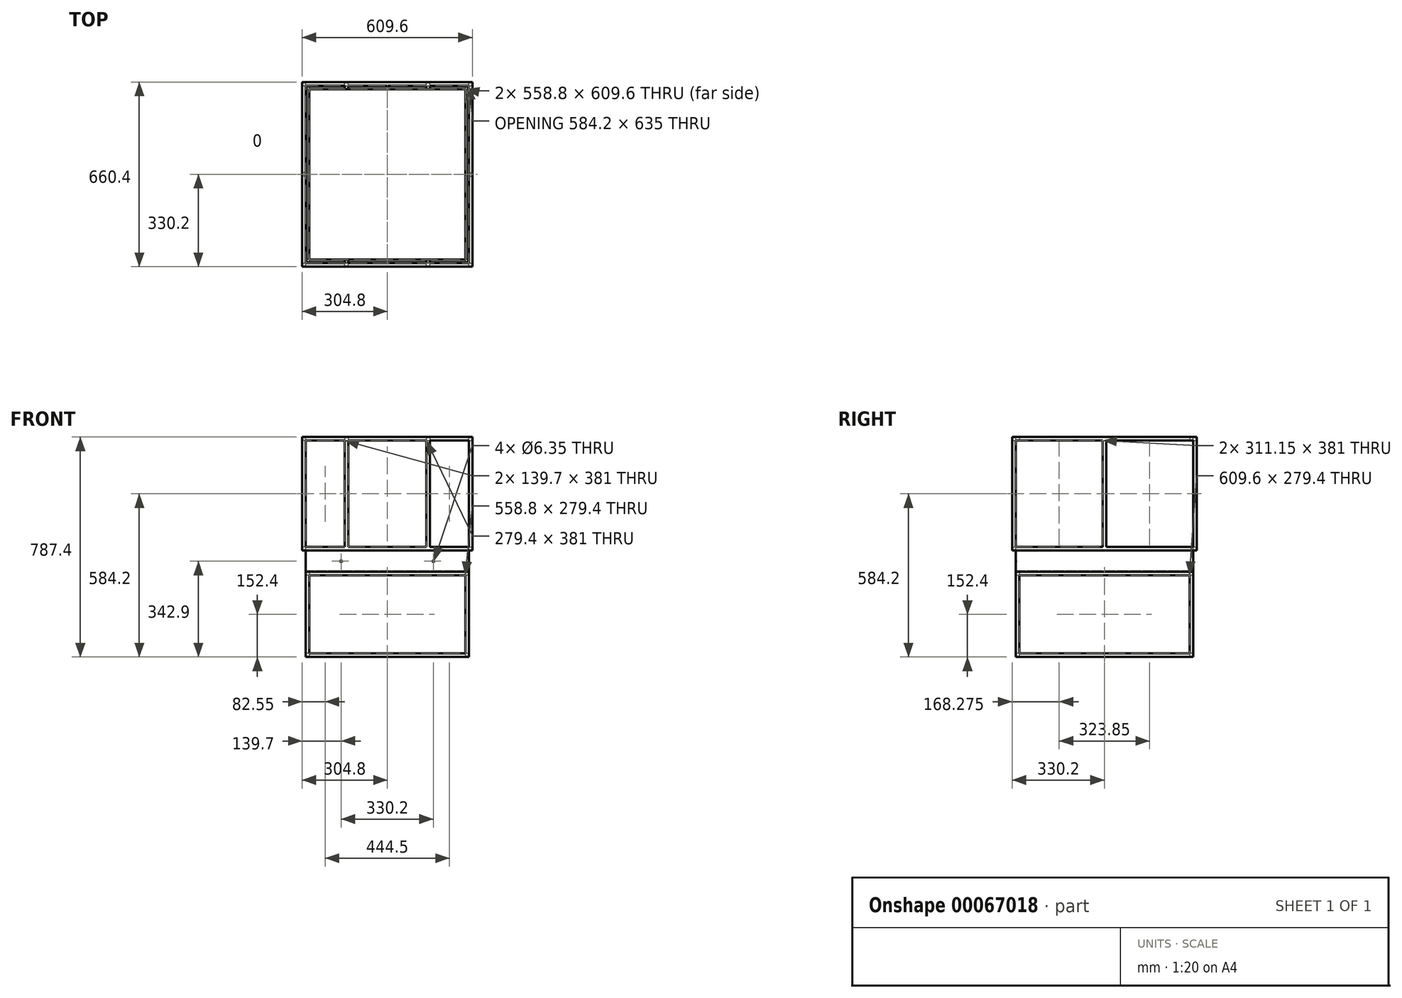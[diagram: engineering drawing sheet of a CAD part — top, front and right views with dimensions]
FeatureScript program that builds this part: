
annotation { "Feature Type Name" : "Feature", "Feature Type Description" : "" }
export const myFeature = defineFeature(function(context is Context, id is Id, definition is map)
    precondition{}
    {
        {
            var Q0;
            Q0=qCreatedBy(makeId("Front.planeOp"),FACE);
            var sketch = newSketch(context, id + "F0", { "sketchPlane" : qUnion([Q0])});
            skLineSegment(sketch, "E0.bottom", {"start": v(0, 0) * mm, "end": v(-609.6, 0) * mm});
            skLineSegment(sketch, "E0.top", {"start": v(0, 406.4) * mm, "end": v(-609.6, 406.4) * mm});
            skLineSegment(sketch, "E0.left", {"start": v(0, 0) * mm, "end": v(0, 406.4) * mm});
            skLineSegment(sketch, "E0.right", {"start": v(-609.6, 0) * mm, "end": v(-609.6, 406.4) * mm});
            skLineSegment(sketch, "E1.bottom", {"start": v(-596.9, 393.7) * mm, "end": v(-457.2, 393.7) * mm});
            skLineSegment(sketch, "E1.top", {"start": v(-596.9, 12.7) * mm, "end": v(-457.2, 12.7) * mm});
            skLineSegment(sketch, "E1.left", {"start": v(-596.9, 393.7) * mm, "end": v(-596.9, 12.7) * mm});
            skLineSegment(sketch, "E1.right", {"start": v(-457.2, 393.7) * mm, "end": v(-457.2, 12.7) * mm});
            skLineSegment(sketch, "E2.bottom", {"start": v(-444.5, 393.7) * mm, "end": v(-165.1, 393.7) * mm});
            skLineSegment(sketch, "E2.top", {"start": v(-444.5, 12.7) * mm, "end": v(-165.1, 12.7) * mm});
            skLineSegment(sketch, "E2.left", {"start": v(-444.5, 393.7) * mm, "end": v(-444.5, 12.7) * mm});
            skLineSegment(sketch, "E2.right", {"start": v(-165.1, 393.7) * mm, "end": v(-165.1, 12.7) * mm});
            skLineSegment(sketch, "E3.bottom", {"start": v(-152.4, 393.7) * mm, "end": v(-12.7, 393.7) * mm});
            skLineSegment(sketch, "E3.top", {"start": v(-152.4, 12.7) * mm, "end": v(-12.7, 12.7) * mm});
            skLineSegment(sketch, "E3.left", {"start": v(-152.4, 393.7) * mm, "end": v(-152.4, 12.7) * mm});
            skLineSegment(sketch, "E3.right", {"start": v(-12.7, 393.7) * mm, "end": v(-12.7, 12.7) * mm});
            skSolve(sketch);
        }
        {
            var Q0;
            Q0=makeQuery(id+"F0.imprint","IMPRINT",FACE,{"disambiguationData":[TD([[makeQuery(id+"F0.imprint","IMPRINT",EDGE,{"derivedFrom":sQuery(id+"F0.wireOp",EDGE,"E0.bottom")}),-1.0]])]});
            extrude(context, id + "F1", {"entities" : qUnion([Q0]), "depth" : 660.4 * mm});
        }
        {
            var Q0;
            Q0=makeQuery(id+"F1.opExtrude","SWEPT_FACE",FACE,{"disambiguationData":[OSD([sQuery(id+"F0.wireOp",EDGE,"E0.top")])]});
            var sketch = newSketch(context, id + "F2", { "sketchPlane" : qUnion([Q0])});
            skLineSegment(sketch, "E4.0", {"start": v(-596.9, -660.4) * mm, "end": v(-596.9, 0) * mm});
            skLineSegment(sketch, "E4.1", {"start": v(-444.5, -660.4) * mm, "end": v(-444.5, 0) * mm});
            skLineSegment(sketch, "E4.2", {"start": v(-152.4, -660.4) * mm, "end": v(-152.4, 0) * mm});
            skLineSegment(sketch, "E4.3", {"start": v(-457.2, -660.4) * mm, "end": v(-457.2, 0) * mm});
            skLineSegment(sketch, "E4.4", {"start": v(-165.1, -660.4) * mm, "end": v(-165.1, 0) * mm});
            skLineSegment(sketch, "E4.5", {"start": v(-12.7, -660.4) * mm, "end": v(-12.7, 0) * mm});
            skLineSegment(sketch, "E4.6", {"start": v(-609.6, -660.4) * mm, "end": v(-609.6, 0) * mm});
            skLineSegment(sketch, "E4.7", {"start": v(0, -660.4) * mm, "end": v(-609.6, -660.4) * mm});
            skLineSegment(sketch, "E4.8", {"start": v(0, -660.4) * mm, "end": v(0, 0) * mm});
            skLineSegment(sketch, "E4.9", {"start": v(0, 0) * mm, "end": v(-609.6, 0) * mm});
            skLineSegment(sketch, "E5", {"start": v(-609.6, -12.7) * mm, "end": v(0, -12.7) * mm});
            skLineSegment(sketch, "E6", {"start": v(-609.6, -647.7) * mm, "end": v(0, -647.7) * mm});
            skLineSegment(sketch, "E7", {"start": v(-609.6, -165.1) * mm, "end": v(0, -165.1) * mm});
            skLineSegment(sketch, "E8", {"start": v(-609.6, -495.3) * mm, "end": v(0, -495.3) * mm});
            skLineSegment(sketch, "E9", {"start": v(-609.6, -177.8) * mm, "end": v(0, -177.8) * mm});
            skLineSegment(sketch, "E10", {"start": v(-609.6, -482.6) * mm, "end": v(0, -482.6) * mm});
            skSolve(sketch);
        }
        {
            var Q0;
            {var subQ0=sQuery(id+"F2.wireOp",EDGE,"E7");var subQ1=sQuery(id+"F2.wireOp",EDGE,"E4.0");var subQ2=makeQuery(id+"F2.imprint","INTERSECT",VERTEX,{"derivedFrom":[subQ1,subQ0]});Q0=makeQuery(id+"F2.imprint","IMPRINT",FACE,{"disambiguationData":[TD([[makeQuery(id+"F2.imprint","IMPRINT",EDGE,{"disambiguationData":[TD([[subQ2,-1.0]])],"derivedFrom":subQ1}),-1.0]])]});}
            var Q1;
            {var subQ0=sQuery(id+"F2.wireOp",EDGE,"E7");var subQ1=sQuery(id+"F2.wireOp",EDGE,"E4.1");var subQ2=makeQuery(id+"F2.imprint","INTERSECT",VERTEX,{"derivedFrom":[subQ1,subQ0]});Q1=makeQuery(id+"F2.imprint","IMPRINT",FACE,{"disambiguationData":[TD([[makeQuery(id+"F2.imprint","IMPRINT",EDGE,{"disambiguationData":[TD([[subQ2,-1.0]])],"derivedFrom":subQ1}),-1.0]])]});}
            var Q2;
            {var subQ0=sQuery(id+"F2.wireOp",EDGE,"E7");var subQ1=sQuery(id+"F2.wireOp",EDGE,"E4.2");var subQ2=makeQuery(id+"F2.imprint","INTERSECT",VERTEX,{"derivedFrom":[subQ1,subQ0]});Q2=makeQuery(id+"F2.imprint","IMPRINT",FACE,{"disambiguationData":[TD([[makeQuery(id+"F2.imprint","IMPRINT",EDGE,{"disambiguationData":[TD([[subQ2,-1.0]])],"derivedFrom":subQ1}),-1.0]])]});}
            var Q3;
            {var subQ0=sQuery(id+"F2.wireOp",EDGE,"E10");var subQ1=sQuery(id+"F2.wireOp",EDGE,"E4.2");var subQ2=makeQuery(id+"F2.imprint","INTERSECT",VERTEX,{"derivedFrom":[subQ1,subQ0]});Q3=makeQuery(id+"F2.imprint","IMPRINT",FACE,{"disambiguationData":[TD([[makeQuery(id+"F2.imprint","IMPRINT",EDGE,{"disambiguationData":[TD([[subQ2,-1.0]])],"derivedFrom":subQ1}),-1.0]])]});}
            var Q4;
            {var subQ0=sQuery(id+"F2.wireOp",EDGE,"E10");var subQ1=sQuery(id+"F2.wireOp",EDGE,"E4.1");var subQ2=makeQuery(id+"F2.imprint","INTERSECT",VERTEX,{"derivedFrom":[subQ1,subQ0]});Q4=makeQuery(id+"F2.imprint","IMPRINT",FACE,{"disambiguationData":[TD([[makeQuery(id+"F2.imprint","IMPRINT",EDGE,{"disambiguationData":[TD([[subQ2,-1.0]])],"derivedFrom":subQ1}),-1.0]])]});}
            var Q5;
            {var subQ0=sQuery(id+"F2.wireOp",EDGE,"E10");var subQ1=sQuery(id+"F2.wireOp",EDGE,"E4.0");var subQ2=makeQuery(id+"F2.imprint","INTERSECT",VERTEX,{"derivedFrom":[subQ1,subQ0]});Q5=makeQuery(id+"F2.imprint","IMPRINT",FACE,{"disambiguationData":[TD([[makeQuery(id+"F2.imprint","IMPRINT",EDGE,{"disambiguationData":[TD([[subQ2,-1.0]])],"derivedFrom":subQ1}),-1.0]])]});}
            var Q6;
            {var subQ0=sQuery(id+"F2.wireOp",EDGE,"E6");var subQ1=sQuery(id+"F2.wireOp",EDGE,"E4.0");var subQ2=makeQuery(id+"F2.imprint","INTERSECT",VERTEX,{"derivedFrom":[subQ1,subQ0]});Q6=makeQuery(id+"F2.imprint","IMPRINT",FACE,{"disambiguationData":[TD([[makeQuery(id+"F2.imprint","IMPRINT",EDGE,{"disambiguationData":[TD([[subQ2,-1.0]])],"derivedFrom":subQ1}),-1.0]])]});}
            var Q7;
            {var subQ0=sQuery(id+"F2.wireOp",EDGE,"E6");var subQ1=sQuery(id+"F2.wireOp",EDGE,"E4.1");var subQ2=makeQuery(id+"F2.imprint","INTERSECT",VERTEX,{"derivedFrom":[subQ1,subQ0]});Q7=makeQuery(id+"F2.imprint","IMPRINT",FACE,{"disambiguationData":[TD([[makeQuery(id+"F2.imprint","IMPRINT",EDGE,{"disambiguationData":[TD([[subQ2,-1.0]])],"derivedFrom":subQ1}),-1.0]])]});}
            var Q8;
            {var subQ0=sQuery(id+"F2.wireOp",EDGE,"E6");var subQ1=sQuery(id+"F2.wireOp",EDGE,"E4.2");var subQ2=makeQuery(id+"F2.imprint","INTERSECT",VERTEX,{"derivedFrom":[subQ1,subQ0]});Q8=makeQuery(id+"F2.imprint","IMPRINT",FACE,{"disambiguationData":[TD([[makeQuery(id+"F2.imprint","IMPRINT",EDGE,{"disambiguationData":[TD([[subQ2,-1.0]])],"derivedFrom":subQ1}),-1.0]])]});}
            extrude(context, id + "F3", {"entities" : qUnion([Q0, Q1, Q2, Q3, Q4, Q5, Q6, Q7, Q8]), "operationType" : NewBodyOperationType.REMOVE, "endBound" : BoundingType.THROUGH_ALL, "oppositeDirection" : true, "depth" : 25.4 * mm});
        }
        {
            var Q0;
            Q0=makeQuery(id+"F1.opExtrude","SWEPT_FACE",FACE,{"disambiguationData":[OSD([sQuery(id+"F0.wireOp",EDGE,"E0.left")])]});
            var sketch = newSketch(context, id + "F4", { "sketchPlane" : qUnion([Q0])});
            skLineSegment(sketch, "E11.0.0", {"start": v(0, 393.7) * mm, "end": v(-12.7, 393.7) * mm});
            skLineSegment(sketch, "E11.0.1", {"start": v(-12.7, 393.7) * mm, "end": v(-12.7, 406.4) * mm});
            skLineSegment(sketch, "E11.0.2", {"start": v(-12.7, 406.4) * mm, "end": v(-165.1, 406.4) * mm});
            skLineSegment(sketch, "E11.0.3", {"start": v(-165.1, 406.4) * mm, "end": v(-165.1, 393.7) * mm});
            skLineSegment(sketch, "E11.0.4", {"start": v(-165.1, 393.7) * mm, "end": v(-177.8, 393.7) * mm});
            skLineSegment(sketch, "E11.0.5", {"start": v(-177.8, 393.7) * mm, "end": v(-177.8, 406.4) * mm});
            skLineSegment(sketch, "E11.0.6", {"start": v(-177.8, 406.4) * mm, "end": v(-482.6, 406.4) * mm});
            skLineSegment(sketch, "E11.0.7", {"start": v(-482.6, 406.4) * mm, "end": v(-482.6, 393.7) * mm});
            skLineSegment(sketch, "E11.0.8", {"start": v(-482.6, 393.7) * mm, "end": v(-495.3, 393.7) * mm});
            skLineSegment(sketch, "E11.0.9", {"start": v(-495.3, 393.7) * mm, "end": v(-495.3, 406.4) * mm});
            skLineSegment(sketch, "E11.0.10", {"start": v(-495.3, 406.4) * mm, "end": v(-647.7, 406.4) * mm});
            skLineSegment(sketch, "E11.0.11", {"start": v(-647.7, 406.4) * mm, "end": v(-647.7, 393.7) * mm});
            skLineSegment(sketch, "E11.0.12", {"start": v(-647.7, 393.7) * mm, "end": v(-660.4, 393.7) * mm});
            skLineSegment(sketch, "E11.0.13", {"start": v(-660.4, 393.7) * mm, "end": v(-660.4, 12.7) * mm});
            skLineSegment(sketch, "E11.0.14", {"start": v(-660.4, 12.7) * mm, "end": v(-647.7, 12.7) * mm});
            skLineSegment(sketch, "E11.0.15", {"start": v(-647.7, 12.7) * mm, "end": v(-647.7, 0) * mm});
            skLineSegment(sketch, "E11.0.16", {"start": v(-647.7, 0) * mm, "end": v(-495.3, 0) * mm});
            skLineSegment(sketch, "E11.0.17", {"start": v(-495.3, 0) * mm, "end": v(-495.3, 12.7) * mm});
            skLineSegment(sketch, "E11.0.18", {"start": v(-495.3, 12.7) * mm, "end": v(-482.6, 12.7) * mm});
            skLineSegment(sketch, "E11.0.19", {"start": v(-482.6, 12.7) * mm, "end": v(-482.6, 0) * mm});
            skLineSegment(sketch, "E11.0.20", {"start": v(-482.6, 0) * mm, "end": v(-177.8, 0) * mm});
            skLineSegment(sketch, "E11.0.21", {"start": v(-177.8, 0) * mm, "end": v(-177.8, 12.7) * mm});
            skLineSegment(sketch, "E11.0.22", {"start": v(-177.8, 12.7) * mm, "end": v(-165.1, 12.7) * mm});
            skLineSegment(sketch, "E11.0.23", {"start": v(-165.1, 12.7) * mm, "end": v(-165.1, 0) * mm});
            skLineSegment(sketch, "E11.0.24", {"start": v(-165.1, 0) * mm, "end": v(-12.7, 0) * mm});
            skLineSegment(sketch, "E11.0.25", {"start": v(-12.7, 0) * mm, "end": v(-12.7, 12.7) * mm});
            skLineSegment(sketch, "E11.0.26", {"start": v(-12.7, 12.7) * mm, "end": v(0, 12.7) * mm});
            skLineSegment(sketch, "E11.0.27", {"start": v(0, 12.7) * mm, "end": v(0, 393.7) * mm});
            skLineSegment(sketch, "E12", {"start": v(-647.7, 393.7) * mm, "end": v(-12.7, 393.7) * mm});
            skLineSegment(sketch, "E13", {"start": v(-12.7, 393.7) * mm, "end": v(-12.7, 12.7) * mm});
            skLineSegment(sketch, "E14", {"start": v(-12.7, 12.7) * mm, "end": v(-647.7, 12.7) * mm});
            skLineSegment(sketch, "E15", {"start": v(-647.7, 12.7) * mm, "end": v(-647.7, 393.7) * mm});
            skLineSegment(sketch, "E16", {"start": v(-495.3, 393.7) * mm, "end": v(-495.3, 12.7) * mm});
            skLineSegment(sketch, "E17", {"start": v(-482.6, 12.7) * mm, "end": v(-482.6, 393.7) * mm});
            skLineSegment(sketch, "E18", {"start": v(-177.8, 393.7) * mm, "end": v(-177.8, 12.7) * mm});
            skLineSegment(sketch, "E19", {"start": v(-165.1, 393.7) * mm, "end": v(-165.1, 12.7) * mm});
            skSolve(sketch);
        }
        {
            var Q0;
            {var subQ2=sQuery(id+"F4.wireOp",EDGE,"E15");Q0=makeQuery(id+"F4.imprint","IMPRINT",FACE,{"disambiguationData":[TD([[makeQuery(id+"F4.imprint","IMPRINT",EDGE,{"derivedFrom":subQ2}),-1.0]])]});}
            var Q1;
            {var subQ2=sQuery(id+"F4.wireOp",EDGE,"E17");Q1=makeQuery(id+"F4.imprint","IMPRINT",FACE,{"disambiguationData":[TD([[makeQuery(id+"F4.imprint","IMPRINT",EDGE,{"derivedFrom":subQ2}),-1.0]])]});}
            var Q2;
            {var subQ0=sQuery(id+"F4.wireOp",EDGE,"E13");Q2=makeQuery(id+"F4.imprint","IMPRINT",FACE,{"disambiguationData":[TD([[makeQuery(id+"F4.imprint","IMPRINT",EDGE,{"derivedFrom":subQ0}),-1.0]])]});}
            extrude(context, id + "F5", {"entities" : qUnion([Q0, Q1, Q2]), "operationType" : NewBodyOperationType.REMOVE, "endBound" : BoundingType.THROUGH_ALL, "oppositeDirection" : true, "depth" : 25.4 * mm});
        }
        {
            var Q0;
            {var subQ1=sQuery(id+"F2.wireOp",EDGE,"E6");var subQ3=sQuery(id+"F2.wireOp",EDGE,"E8");var subQ6=makeQuery(id+"F1.opExtrude","SWEPT_FACE",FACE,{"disambiguationData":[OSD([sQuery(id+"F0.wireOp",EDGE,"E3.left")])]});var subQ7=sQuery(id+"F2.wireOp",EDGE,"E10");var subQ8=sQuery(id+"F2.wireOp",EDGE,"E4.2");var subQ9=makeQuery(id+"F2.imprint","INTERSECT",VERTEX,{"derivedFrom":[subQ8,subQ7]});var subQ11=makeQuery(id+"F3.opExtrude","SWEPT_FACE",FACE,{"disambiguationData":[OSD([subQ8]),TDD([makeQuery(id+"F2.imprint","IMPRINT",EDGE,{"disambiguationData":[TD([[subQ9,-1.0]])],"derivedFrom":subQ8})])]});var subQ12=makeQuery(id+"F1.opExtrude","SWEPT_FACE",FACE,{"disambiguationData":[OSD([sQuery(id+"F0.wireOp",EDGE,"E3.top")])]});var subQ13=makeQuery(id+"F1.opExtrude","SWEPT_FACE",FACE,{"disambiguationData":[OSD([sQuery(id+"F0.wireOp",EDGE,"E0.bottom")])]});var subQ16=makeQuery(id+"F2.imprint","INTERSECT",VERTEX,{"derivedFrom":[subQ8,subQ3]});var subQ17=makeQuery(id+"F3.opExtrude","SWEPT_FACE",FACE,{"disambiguationData":[OSD([subQ8]),TDD([makeQuery(id+"F2.imprint","IMPRINT",EDGE,{"disambiguationData":[TD([[makeQuery(id+"F2.imprint","INTERSECT",VERTEX,{"derivedFrom":[subQ8,subQ1]}),-1.0]])],"derivedFrom":subQ8})])]});var subQ18=sQuery(id+"F2.wireOp",EDGE,"E7");var subQ21=makeQuery(id+"F3.opExtrude","SWEPT_FACE",FACE,{"disambiguationData":[OSD([subQ8]),TDD([makeQuery(id+"F2.imprint","IMPRINT",EDGE,{"disambiguationData":[TD([[makeQuery(id+"F2.imprint","INTERSECT",VERTEX,{"derivedFrom":[subQ8,subQ18]}),-1.0]])],"derivedFrom":subQ8})])]});var subQ22=makeQuery(id+"F3.opExtrude","SWEPT_FACE",FACE,{"disambiguationData":[OSD([subQ7]),TDD([makeQuery(id+"F2.imprint","IMPRINT",EDGE,{"disambiguationData":[TD([[subQ9,-1.0]])],"derivedFrom":subQ7})])]});var subQ23=makeQuery(id+"F1.opExtrude","SWEPT_FACE",FACE,{"disambiguationData":[OSD([sQuery(id+"F0.wireOp",EDGE,"E3.bottom")])]});var subQ24=makeQuery(id+"F1.opExtrude","SWEPT_FACE",FACE,{"disambiguationData":[OSD([sQuery(id+"F0.wireOp",EDGE,"E0.top")])]});var subQ25=makeQuery(id+"F3.opExtrude","SWEPT_FACE",FACE,{"disambiguationData":[OSD([subQ3]),TDD([makeQuery(id+"F2.imprint","IMPRINT",EDGE,{"disambiguationData":[TD([[subQ16,-1.0]])],"derivedFrom":subQ3})])]});var subQ26=sQuery(id+"F4.wireOp",EDGE,"E17");var subQ27=sQuery(id+"F4.wireOp",EDGE,"E18");var subQ28=sQuery(id+"F4.wireOp",EDGE,"E12");var subQ30=sQuery(id+"F4.wireOp",EDGE,"E14");var subQ31=sQuery(id+"F4.wireOp",EDGE,"E16");Q0=makeQuery(id+"F5.boolean.opBoolean","SPLIT",FACE,{"disambiguationData":[TD([subQ23,subQ12,subQ6,subQ17,subQ11,subQ21,makeQuery(id+"F3.boolean.opBoolean","COPY",FACE,{"disambiguationData":[TD([subQ24])],"derivedFrom":subQ25}),makeQuery(id+"F3.boolean.opBoolean","COPY",FACE,{"disambiguationData":[TD([subQ13])],"derivedFrom":subQ25}),makeQuery(id+"F3.boolean.opBoolean","COPY",FACE,{"disambiguationData":[TD([subQ24])],"derivedFrom":subQ22}),makeQuery(id+"F3.boolean.opBoolean","COPY",FACE,{"disambiguationData":[TD([subQ13])],"derivedFrom":subQ22}),makeQuery(id+"F5.opExtrude","SWEPT_FACE",FACE,{"disambiguationData":[OSD([subQ28]),TDD([makeQuery(id+"F4.imprint","IMPRINT",EDGE,{"disambiguationData":[TD([[makeQuery(id+"F4.imprint","INTERSECT",VERTEX,{"derivedFrom":[sQuery(id+"F4.wireOp",EDGE,"E11.0.9"),subQ28,subQ31]}),1.0]])],"derivedFrom":subQ28})])]}),makeQuery(id+"F5.opExtrude","SWEPT_FACE",FACE,{"disambiguationData":[OSD([subQ28]),TDD([makeQuery(id+"F4.imprint","IMPRINT",EDGE,{"disambiguationData":[TD([[makeQuery(id+"F4.imprint","INTERSECT",VERTEX,{"derivedFrom":[sQuery(id+"F4.wireOp",EDGE,"E11.0.5"),subQ28,subQ27]}),1.0]])],"derivedFrom":subQ28})])]}),makeQuery(id+"F5.opExtrude","SWEPT_FACE",FACE,{"disambiguationData":[OSD([subQ30]),TDD([makeQuery(id+"F4.imprint","IMPRINT",EDGE,{"disambiguationData":[TD([[makeQuery(id+"F4.imprint","INTERSECT",VERTEX,{"derivedFrom":[sQuery(id+"F4.wireOp",EDGE,"E11.0.19"),subQ30,subQ26]}),1.0]])],"derivedFrom":subQ30})])]}),makeQuery(id+"F5.opExtrude","SWEPT_FACE",FACE,{"disambiguationData":[OSD([subQ30]),TDD([makeQuery(id+"F4.imprint","IMPRINT",EDGE,{"disambiguationData":[TD([[makeQuery(id+"F4.imprint","INTERSECT",VERTEX,{"derivedFrom":[sQuery(id+"F4.wireOp",EDGE,"E11.0.17"),subQ30,subQ31]}),-1.0]])],"derivedFrom":subQ30})])]}),makeQuery(id+"F5.opExtrude","SWEPT_FACE",FACE,{"disambiguationData":[OSD([subQ31])]}),makeQuery(id+"F5.opExtrude","SWEPT_FACE",FACE,{"disambiguationData":[OSD([subQ26])]})])],"derivedFrom":makeQuery(id+"F3.boolean.opBoolean","MERGE",FACE,{"derivedFrom":[subQ6,subQ17,subQ11,subQ21]})});}
            var sketch = newSketch(context, id + "F6", { "sketchPlane" : qUnion([Q0])});
            skPoint(sketch, "E20.0", {"position": v(-495.3, 12.7) * mm});
            skPoint(sketch, "E20.1", {"position": v(-482.6, 12.7) * mm});
            skLineSegment(sketch, "E20.2", {"start": v(-495.3, 393.7) * mm, "end": v(-495.3, 12.7) * mm});
            skLineSegment(sketch, "E20.3", {"start": v(-482.6, 12.7) * mm, "end": v(-482.6, 393.7) * mm});
            skLineSegment(sketch, "E20.4", {"start": v(-495.3, 12.7) * mm, "end": v(-482.6, 12.7) * mm});
            skLineSegment(sketch, "E20.5", {"start": v(-495.3, 393.7) * mm, "end": v(-482.6, 393.7) * mm});
            skLineSegment(sketch, "E21.0", {"start": v(-177.8, 393.7) * mm, "end": v(-165.1, 393.7) * mm});
            skLineSegment(sketch, "E21.1", {"start": v(-177.8, 393.7) * mm, "end": v(-177.8, 12.7) * mm});
            skLineSegment(sketch, "E21.2", {"start": v(-165.1, 393.7) * mm, "end": v(-165.1, 12.7) * mm});
            skLineSegment(sketch, "E21.3", {"start": v(-177.8, 12.7) * mm, "end": v(-165.1, 12.7) * mm});
            skSolve(sketch);
        }
        {
            var Q0;
            Q0=makeQuery(id+"F6.imprint","IMPRINT",FACE,{"disambiguationData":[TD([[makeQuery(id+"F6.imprint","IMPRINT",EDGE,{"derivedFrom":sQuery(id+"F6.wireOp",EDGE,"E20.2")}),1.0]])]});
            var Q1;
            Q1=makeQuery(id+"F6.imprint","IMPRINT",FACE,{"disambiguationData":[TD([[makeQuery(id+"F6.imprint","IMPRINT",EDGE,{"derivedFrom":sQuery(id+"F6.wireOp",EDGE,"E21.0")}),-1.0]])]});
            extrude(context, id + "F7", {"entities" : qUnion([Q0, Q1]), "operationType" : NewBodyOperationType.REMOVE, "oppositeDirection" : true, "depth" : 304.8 * mm});
        }
        {
            var Q0;
            Q0=makeQuery(id+"F1.opExtrude","SWEPT_FACE",FACE,{"disambiguationData":[OSD([sQuery(id+"F0.wireOp",EDGE,"E0.top")])]});
            var sketch = newSketch(context, id + "F8", { "sketchPlane" : qUnion([Q0])});
            skLineSegment(sketch, "E22.0", {"start": v(-596.9, -165.1) * mm, "end": v(-457.2, -165.1) * mm});
            skLineSegment(sketch, "E22.1", {"start": v(-596.9, -177.8) * mm, "end": v(-457.2, -177.8) * mm});
            skLineSegment(sketch, "E22.2", {"start": v(-444.5, -165.1) * mm, "end": v(-165.1, -165.1) * mm});
            skLineSegment(sketch, "E22.3", {"start": v(-444.5, -177.8) * mm, "end": v(-165.1, -177.8) * mm});
            skLineSegment(sketch, "E22.4", {"start": v(-152.4, -165.1) * mm, "end": v(-12.7, -165.1) * mm});
            skLineSegment(sketch, "E22.5", {"start": v(-152.4, -177.8) * mm, "end": v(-12.7, -177.8) * mm});
            skLineSegment(sketch, "E22.6", {"start": v(-596.9, -482.6) * mm, "end": v(-457.2, -482.6) * mm});
            skLineSegment(sketch, "E22.7", {"start": v(-596.9, -495.3) * mm, "end": v(-457.2, -495.3) * mm});
            skLineSegment(sketch, "E22.8", {"start": v(-444.5, -482.6) * mm, "end": v(-165.1, -482.6) * mm});
            skLineSegment(sketch, "E22.9", {"start": v(-444.5, -495.3) * mm, "end": v(-165.1, -495.3) * mm});
            skLineSegment(sketch, "E22.10", {"start": v(-152.4, -482.6) * mm, "end": v(-12.7, -482.6) * mm});
            skLineSegment(sketch, "E22.11", {"start": v(-152.4, -495.3) * mm, "end": v(-12.7, -495.3) * mm});
            skLineSegment(sketch, "E23", {"start": v(-596.9, -482.6) * mm, "end": v(-596.9, -495.3) * mm});
            skLineSegment(sketch, "E24", {"start": v(-457.2, -482.6) * mm, "end": v(-457.2, -495.3) * mm});
            skLineSegment(sketch, "E25", {"start": v(-444.5, -495.3) * mm, "end": v(-444.5, -482.6) * mm});
            skLineSegment(sketch, "E26", {"start": v(-165.1, -482.6) * mm, "end": v(-165.1, -495.3) * mm});
            skLineSegment(sketch, "E27", {"start": v(-152.4, -495.3) * mm, "end": v(-152.4, -482.6) * mm});
            skLineSegment(sketch, "E28", {"start": v(-12.7, -482.6) * mm, "end": v(-12.7, -495.3) * mm});
            skLineSegment(sketch, "E29", {"start": v(-596.9, -165.1) * mm, "end": v(-596.9, -177.8) * mm});
            skLineSegment(sketch, "E30", {"start": v(-457.2, -165.1) * mm, "end": v(-457.2, -177.8) * mm});
            skLineSegment(sketch, "E31", {"start": v(-444.5, -165.1) * mm, "end": v(-444.5, -177.8) * mm});
            skLineSegment(sketch, "E32", {"start": v(-165.1, -165.1) * mm, "end": v(-165.1, -177.8) * mm});
            skLineSegment(sketch, "E33", {"start": v(-152.4, -165.1) * mm, "end": v(-152.4, -177.8) * mm});
            skLineSegment(sketch, "E34", {"start": v(-12.7, -177.8) * mm, "end": v(-12.7, -165.1) * mm});
            skSolve(sketch);
        }
        {
            var Q0;
            Q0=makeQuery(id+"F8.imprint","IMPRINT",FACE,{"disambiguationData":[TD([[makeQuery(id+"F8.imprint","IMPRINT",EDGE,{"derivedFrom":sQuery(id+"F8.wireOp",EDGE,"E22.0")}),-1.0]])]});
            var Q1;
            Q1=makeQuery(id+"F8.imprint","IMPRINT",FACE,{"disambiguationData":[TD([[makeQuery(id+"F8.imprint","IMPRINT",EDGE,{"derivedFrom":sQuery(id+"F8.wireOp",EDGE,"E22.2")}),-1.0]])]});
            var Q2;
            Q2=makeQuery(id+"F8.imprint","IMPRINT",FACE,{"disambiguationData":[TD([[makeQuery(id+"F8.imprint","IMPRINT",EDGE,{"derivedFrom":sQuery(id+"F8.wireOp",EDGE,"E22.4")}),-1.0]])]});
            var Q3;
            Q3=makeQuery(id+"F8.imprint","IMPRINT",FACE,{"disambiguationData":[TD([[makeQuery(id+"F8.imprint","IMPRINT",EDGE,{"derivedFrom":sQuery(id+"F8.wireOp",EDGE,"E22.10")}),-1.0]])]});
            var Q4;
            Q4=makeQuery(id+"F8.imprint","IMPRINT",FACE,{"disambiguationData":[TD([[makeQuery(id+"F8.imprint","IMPRINT",EDGE,{"derivedFrom":sQuery(id+"F8.wireOp",EDGE,"E22.8")}),-1.0]])]});
            var Q5;
            Q5=makeQuery(id+"F8.imprint","IMPRINT",FACE,{"disambiguationData":[TD([[makeQuery(id+"F8.imprint","IMPRINT",EDGE,{"derivedFrom":sQuery(id+"F8.wireOp",EDGE,"E22.6")}),-1.0]])]});
            extrude(context, id + "F9", {"entities" : qUnion([Q0, Q1, Q2, Q3, Q4, Q5]), "operationType" : NewBodyOperationType.REMOVE, "endBound" : BoundingType.THROUGH_ALL, "oppositeDirection" : true, "depth" : 25.4 * mm});
        }
        {
            var Q0;
            Q0=makeQuery(id+"F1.opExtrude","SWEPT_FACE",FACE,{"disambiguationData":[OSD([sQuery(id+"F0.wireOp",EDGE,"E0.bottom")])]});
            var sketch = newSketch(context, id + "F10", { "sketchPlane" : qUnion([Q0])});
            skLineSegment(sketch, "E35.0", {"start": v(-457.2, 12.7) * mm, "end": v(-457.2, 647.7) * mm});
            skLineSegment(sketch, "E35.1", {"start": v(-444.5, 12.7) * mm, "end": v(-444.5, 647.7) * mm});
            skLineSegment(sketch, "E35.2", {"start": v(-165.1, 12.7) * mm, "end": v(-165.1, 647.7) * mm});
            skLineSegment(sketch, "E35.3", {"start": v(-152.4, 12.7) * mm, "end": v(-152.4, 647.7) * mm});
            skLineSegment(sketch, "E36", {"start": v(-457.2, 12.7) * mm, "end": v(-444.5, 12.7) * mm});
            skLineSegment(sketch, "E37", {"start": v(-165.1, 12.7) * mm, "end": v(-152.4, 12.7) * mm});
            skLineSegment(sketch, "E38", {"start": v(-152.4, 647.7) * mm, "end": v(-165.1, 647.7) * mm});
            skLineSegment(sketch, "E39", {"start": v(-444.5, 647.7) * mm, "end": v(-457.2, 647.7) * mm});
            skSolve(sketch);
        }
        {
            var Q0;
            Q0=makeQuery(id+"F10.imprint","IMPRINT",FACE,{"disambiguationData":[TD([[makeQuery(id+"F10.imprint","IMPRINT",EDGE,{"derivedFrom":sQuery(id+"F10.wireOp",EDGE,"E35.0")}),-1.0]])]});
            var Q1;
            Q1=makeQuery(id+"F10.imprint","IMPRINT",FACE,{"disambiguationData":[TD([[makeQuery(id+"F10.imprint","IMPRINT",EDGE,{"derivedFrom":sQuery(id+"F10.wireOp",EDGE,"E35.2")}),-1.0]])]});
            extrude(context, id + "F11", {"entities" : qUnion([Q0, Q1]), "operationType" : NewBodyOperationType.REMOVE, "oppositeDirection" : true, "depth" : 25.4 * mm});
        }
        {
            var Q0;
            Q0=makeQuery(id+"F1.opExtrude","SWEPT_FACE",FACE,{"disambiguationData":[OSD([sQuery(id+"F0.wireOp",EDGE,"E0.bottom")])]});
            var sketch = newSketch(context, id + "F12", { "sketchPlane" : qUnion([Q0])});
            skLineSegment(sketch, "E40.0", {"start": v(-12.7, 12.7) * mm, "end": v(-12.7, 647.7) * mm});
            skLineSegment(sketch, "E40.1", {"start": v(-12.7, 647.7) * mm, "end": v(-596.9, 647.7) * mm});
            skLineSegment(sketch, "E40.2", {"start": v(-596.9, 12.7) * mm, "end": v(-596.9, 647.7) * mm});
            skLineSegment(sketch, "E40.3", {"start": v(-12.7, 12.7) * mm, "end": v(-596.9, 12.7) * mm});
            skSolve(sketch);
        }
        {
            var Q0;
            Q0=makeQuery(id+"F12.imprint","IMPRINT",FACE,{"disambiguationData":[TD([[makeQuery(id+"F12.imprint","IMPRINT",EDGE,{"derivedFrom":sQuery(id+"F12.wireOp",EDGE,"E40.0")}),1.0]])]});
            extrude(context, id + "F13", {"entities" : qUnion([Q0]), "depth" : 76.2 * mm});
        }
        {
            var Q0;
            Q0=makeQuery(id+"F13.opExtrude","CAP_FACE",FACE,{"disambiguationData":[OSD([sQuery(id+"F12.wireOp",EDGE,"E40.0"),sQuery(id+"F12.wireOp",EDGE,"E40.1"),sQuery(id+"F12.wireOp",EDGE,"E40.2"),sQuery(id+"F12.wireOp",EDGE,"E40.3")])],"isStart":true});
            shell(context, id + "F14", {"entities" : qUnion([Q0]), "thickness" : 2.54 * mm});
        }
        {
            var Q0;
            Q0=makeQuery(id+"F13.opExtrude","SWEPT_FACE",FACE,{"disambiguationData":[OSD([sQuery(id+"F12.wireOp",EDGE,"E40.1")])]});
            var sketch = newSketch(context, id + "F15", { "sketchPlane" : qUnion([Q0])});
            skLineSegment(sketch, "E41", {"start": v(-596.9, -38.1) * mm, "end": v(-12.7, -38.1) * mm, "construction": true});
            skCircle(sketch, "E42", {"center": v(-469.9, -38.1) * mm, "radius": 3.18 * mm});
            skCircle(sketch, "E43", {"center": v(-139.7, -38.1) * mm, "radius": 3.18 * mm});
            skSolve(sketch);
        }
        {
            var Q0;
            Q0=makeQuery(id+"F15.imprint","IMPRINT",FACE,{"disambiguationData":[TD([[makeQuery(id+"F15.imprint","IMPRINT",EDGE,{"derivedFrom":sQuery(id+"F15.wireOp",EDGE,"E43")}),1.0]])]});
            var Q1;
            Q1=makeQuery(id+"F15.imprint","IMPRINT",FACE,{"disambiguationData":[TD([[makeQuery(id+"F15.imprint","IMPRINT",EDGE,{"derivedFrom":sQuery(id+"F15.wireOp",EDGE,"E42")}),1.0]])]});
            extrude(context, id + "F16", {"entities" : qUnion([Q0, Q1]), "operationType" : NewBodyOperationType.REMOVE, "endBound" : BoundingType.THROUGH_ALL, "oppositeDirection" : true, "depth" : 25.4 * mm});
        }
        {
            var Q0;
            Q0=makeQuery(id+"F13.opExtrude","CAP_FACE",FACE,{"disambiguationData":[OSD([sQuery(id+"F12.wireOp",EDGE,"E40.0"),sQuery(id+"F12.wireOp",EDGE,"E40.1"),sQuery(id+"F12.wireOp",EDGE,"E40.2"),sQuery(id+"F12.wireOp",EDGE,"E40.3")])],"isStart":false});
            var sketch = newSketch(context, id + "F17", { "sketchPlane" : qUnion([Q0])});
            skLineSegment(sketch, "E44.0", {"start": v(-12.7, 647.7) * mm, "end": v(-596.9, 647.7) * mm});
            skLineSegment(sketch, "E44.1", {"start": v(-596.9, 12.7) * mm, "end": v(-596.9, 647.7) * mm});
            skLineSegment(sketch, "E44.2", {"start": v(-12.7, 12.7) * mm, "end": v(-12.7, 647.7) * mm});
            skLineSegment(sketch, "E44.3", {"start": v(-12.7, 12.7) * mm, "end": v(-596.9, 12.7) * mm});
            skSolve(sketch);
        }
        {
            var Q0;
            Q0=makeQuery(id+"F17.imprint","IMPRINT",FACE,{"disambiguationData":[TD([[makeQuery(id+"F17.imprint","IMPRINT",EDGE,{"derivedFrom":sQuery(id+"F17.wireOp",EDGE,"E44.0")}),1.0]])]});
            extrude(context, id + "F18", {"entities" : qUnion([Q0]), "depth" : 304.8 * mm});
        }
        {
            var Q0;
            Q0=makeQuery(id+"F18.opExtrude","SWEPT_FACE",FACE,{"disambiguationData":[OSD([sQuery(id+"F17.wireOp",EDGE,"E44.0")])]});
            var sketch = newSketch(context, id + "F19", { "sketchPlane" : qUnion([Q0])});
            skLineSegment(sketch, "E45.0", {"start": v(-12.7, -76.2) * mm, "end": v(-596.9, -76.2) * mm});
            skLineSegment(sketch, "E45.1", {"start": v(-596.9, -381) * mm, "end": v(-596.9, -76.2) * mm});
            skLineSegment(sketch, "E45.2", {"start": v(-12.7, -381) * mm, "end": v(-596.9, -381) * mm});
            skLineSegment(sketch, "E45.3", {"start": v(-12.7, -381) * mm, "end": v(-12.7, -76.2) * mm});
            skLineSegment(sketch, "E46.0", {"start": v(-584.2, -368.3) * mm, "end": v(-584.2, -88.9) * mm});
            skLineSegment(sketch, "E46.1", {"start": v(-25.4, -368.3) * mm, "end": v(-584.2, -368.3) * mm});
            skLineSegment(sketch, "E46.2", {"start": v(-25.4, -368.3) * mm, "end": v(-25.4, -88.9) * mm});
            skLineSegment(sketch, "E46.3", {"start": v(-25.4, -88.9) * mm, "end": v(-584.2, -88.9) * mm});
            skSolve(sketch);
        }
        {
            var Q0;
            Q0=makeQuery(id+"F19.imprint","IMPRINT",FACE,{"disambiguationData":[TD([[makeQuery(id+"F19.imprint","IMPRINT",EDGE,{"derivedFrom":sQuery(id+"F19.wireOp",EDGE,"E46.0")}),-1.0]])]});
            extrude(context, id + "F20", {"entities" : qUnion([Q0]), "operationType" : NewBodyOperationType.REMOVE, "endBound" : BoundingType.THROUGH_ALL, "oppositeDirection" : true, "depth" : 25.4 * mm});
        }
        {
            var Q0;
            Q0=makeQuery(id+"F18.opExtrude","SWEPT_FACE",FACE,{"disambiguationData":[OSD([sQuery(id+"F17.wireOp",EDGE,"E44.1")])]});
            var sketch = newSketch(context, id + "F21", { "sketchPlane" : qUnion([Q0])});
            skLineSegment(sketch, "E47.0", {"start": v(647.7, -381) * mm, "end": v(647.7, -76.2) * mm});
            skLineSegment(sketch, "E47.1", {"start": v(12.7, -76.2) * mm, "end": v(647.7, -76.2) * mm});
            skLineSegment(sketch, "E47.2", {"start": v(12.7, -381) * mm, "end": v(647.7, -381) * mm});
            skLineSegment(sketch, "E47.3", {"start": v(12.7, -381) * mm, "end": v(12.7, -76.2) * mm});
            skLineSegment(sketch, "E48.0", {"start": v(25.4, -88.9) * mm, "end": v(635, -88.9) * mm});
            skLineSegment(sketch, "E48.1", {"start": v(25.4, -368.3) * mm, "end": v(25.4, -88.9) * mm});
            skLineSegment(sketch, "E48.2", {"start": v(25.4, -368.3) * mm, "end": v(635, -368.3) * mm});
            skLineSegment(sketch, "E48.3", {"start": v(635, -368.3) * mm, "end": v(635, -88.9) * mm});
            skSolve(sketch);
        }
        {
            var Q0;
            Q0=makeQuery(id+"F21.imprint","IMPRINT",FACE,{"disambiguationData":[TD([[makeQuery(id+"F21.imprint","IMPRINT",EDGE,{"derivedFrom":sQuery(id+"F21.wireOp",EDGE,"E48.0")}),-1.0]])]});
            extrude(context, id + "F22", {"entities" : qUnion([Q0]), "operationType" : NewBodyOperationType.REMOVE, "endBound" : BoundingType.THROUGH_ALL, "oppositeDirection" : true, "depth" : 25.4 * mm});
        }
        {
            var Q0;
            Q0=makeQuery(id+"F18.opExtrude","CAP_FACE",FACE,{"disambiguationData":[OSD([sQuery(id+"F17.wireOp",EDGE,"E44.0"),sQuery(id+"F17.wireOp",EDGE,"E44.1"),sQuery(id+"F17.wireOp",EDGE,"E44.2"),sQuery(id+"F17.wireOp",EDGE,"E44.3")])],"isStart":false});
            var sketch = newSketch(context, id + "F23", { "sketchPlane" : qUnion([Q0])});
            skLineSegment(sketch, "E49.0", {"start": v(-12.7, 647.7) * mm, "end": v(-596.9, 647.7) * mm});
            skLineSegment(sketch, "E49.1", {"start": v(-596.9, 12.7) * mm, "end": v(-596.9, 647.7) * mm});
            skLineSegment(sketch, "E49.2", {"start": v(-12.7, 25.4) * mm, "end": v(-12.7, 635) * mm});
            skLineSegment(sketch, "E49.3", {"start": v(-12.7, 12.7) * mm, "end": v(-596.9, 12.7) * mm});
            skLineSegment(sketch, "E49.4", {"start": v(-12.7, 12.7) * mm, "end": v(-12.7, 647.7) * mm});
            skLineSegment(sketch, "E50.0", {"start": v(-584.2, 25.4) * mm, "end": v(-584.2, 635) * mm});
            skLineSegment(sketch, "E50.1", {"start": v(-25.4, 25.4) * mm, "end": v(-584.2, 25.4) * mm});
            skLineSegment(sketch, "E50.2", {"start": v(-25.4, 25.4) * mm, "end": v(-25.4, 635) * mm});
            skLineSegment(sketch, "E50.3", {"start": v(-25.4, 635) * mm, "end": v(-584.2, 635) * mm});
            skSolve(sketch);
        }
        {
            var Q0;
            Q0=makeQuery(id+"F23.imprint","IMPRINT",FACE,{"disambiguationData":[TD([[makeQuery(id+"F23.imprint","IMPRINT",EDGE,{"derivedFrom":sQuery(id+"F23.wireOp",EDGE,"E50.0")}),-1.0]])]});
            extrude(context, id + "F24", {"entities" : qUnion([Q0]), "operationType" : NewBodyOperationType.REMOVE, "endBound" : BoundingType.THROUGH_ALL, "oppositeDirection" : true, "depth" : 25.4 * mm});
        }
        {
            var Q0;
            Q0=makeQuery(id+"F1.opExtrude","SWEPT_FACE",FACE,{"disambiguationData":[OSD([sQuery(id+"F0.wireOp",EDGE,"E0.left")])]});
            var sketch = newSketch(context, id + "F25", { "sketchPlane" : qUnion([Q0])});
            skLineSegment(sketch, "E51.0", {"start": v(-495.3, 393.7) * mm, "end": v(-495.3, 12.7) * mm});
            skLineSegment(sketch, "E51.1", {"start": v(-482.6, 12.7) * mm, "end": v(-482.6, 393.7) * mm});
            skLineSegment(sketch, "E51.2", {"start": v(-165.1, 393.7) * mm, "end": v(-165.1, 12.7) * mm});
            skLineSegment(sketch, "E51.3", {"start": v(-177.8, 393.7) * mm, "end": v(-177.8, 12.7) * mm});
            skLineSegment(sketch, "E52", {"start": v(-495.3, 393.7) * mm, "end": v(-482.6, 393.7) * mm});
            skLineSegment(sketch, "E53", {"start": v(-177.8, 393.7) * mm, "end": v(-165.1, 393.7) * mm});
            skLineSegment(sketch, "E54", {"start": v(-165.1, 12.7) * mm, "end": v(-177.8, 12.7) * mm});
            skLineSegment(sketch, "E55", {"start": v(-495.3, 12.7) * mm, "end": v(-482.6, 12.7) * mm});
            skSolve(sketch);
        }
        {
            var Q0;
            Q0=makeQuery(id+"F25.imprint","IMPRINT",FACE,{"disambiguationData":[TD([[makeQuery(id+"F25.imprint","IMPRINT",EDGE,{"derivedFrom":sQuery(id+"F25.wireOp",EDGE,"E51.0")}),1.0]])]});
            var Q1;
            Q1=makeQuery(id+"F25.imprint","IMPRINT",FACE,{"disambiguationData":[TD([[makeQuery(id+"F25.imprint","IMPRINT",EDGE,{"derivedFrom":sQuery(id+"F25.wireOp",EDGE,"E51.2")}),-1.0]])]});
            extrude(context, id + "F26", {"entities" : qUnion([Q0, Q1]), "operationType" : NewBodyOperationType.REMOVE, "endBound" : BoundingType.THROUGH_ALL, "oppositeDirection" : true, "depth" : 25.4 * mm});
        }
        {
            var Q0;
            Q0=makeQuery(id+"F1.opExtrude","SWEPT_FACE",FACE,{"disambiguationData":[OSD([sQuery(id+"F0.wireOp",EDGE,"E0.left")])]});
            var sketch = newSketch(context, id + "F27", { "sketchPlane" : qUnion([Q0])});
            skLineSegment(sketch, "E56.0", {"start": v(-660.4, 406.4) * mm, "end": v(0, 406.4) * mm});
            skLineSegment(sketch, "E56.1", {"start": v(-660.4, 0) * mm, "end": v(-660.4, 406.4) * mm});
            skLineSegment(sketch, "E56.2", {"start": v(-647.7, 12.7) * mm, "end": v(-647.7, 393.7) * mm});
            skLineSegment(sketch, "E56.3", {"start": v(-647.7, 393.7) * mm, "end": v(-12.7, 393.7) * mm});
            skLineSegment(sketch, "E56.4", {"start": v(-12.7, 393.7) * mm, "end": v(-12.7, 12.7) * mm});
            skLineSegment(sketch, "E56.5", {"start": v(0, 0) * mm, "end": v(0, 406.4) * mm});
            skLineSegment(sketch, "E56.6", {"start": v(-660.4, 0) * mm, "end": v(0, 0) * mm});
            skLineSegment(sketch, "E56.7", {"start": v(-12.7, 12.7) * mm, "end": v(-647.7, 12.7) * mm});
            skLineSegment(sketch, "E57", {"start": v(-330.2, 393.7) * mm, "end": v(-330.2, 12.7) * mm, "construction": true});
            skLineSegment(sketch, "E58", {"start": v(-323.85, 393.7) * mm, "end": v(-323.85, 12.7) * mm});
            skLineSegment(sketch, "E59", {"start": v(-336.55, 393.7) * mm, "end": v(-336.55, 12.7) * mm});
            skSolve(sketch);
        }
        {
            var Q0;
            {var subQ0=sQuery(id+"F27.wireOp",EDGE,"E58");Q0=makeQuery(id+"F27.imprint","IMPRINT",FACE,{"disambiguationData":[TD([[makeQuery(id+"F27.imprint","IMPRINT",EDGE,{"derivedFrom":subQ0}),-1.0]])]});}
            extrude(context, id + "F28", {"entities" : qUnion([Q0]), "operationType" : NewBodyOperationType.ADD, "oppositeDirection" : true, "depth" : 12.7 * mm});
        }
        {
            var Q0;
            Q0=makeQuery(id+"F1.opExtrude","SWEPT_FACE",FACE,{"disambiguationData":[OSD([sQuery(id+"F0.wireOp",EDGE,"E0.right")])]});
            var sketch = newSketch(context, id + "F29", { "sketchPlane" : qUnion([Q0])});
            skLineSegment(sketch, "E60.0", {"start": v(336.55, 393.7) * mm, "end": v(336.55, 12.7) * mm});
            skLineSegment(sketch, "E60.1", {"start": v(323.85, 393.7) * mm, "end": v(323.85, 12.7) * mm});
            skLineSegment(sketch, "E61", {"start": v(323.85, 393.7) * mm, "end": v(336.55, 393.7) * mm});
            skLineSegment(sketch, "E62", {"start": v(323.85, 12.7) * mm, "end": v(336.55, 12.7) * mm});
            skSolve(sketch);
        }
        {
            var Q0;
            Q0=makeQuery(id+"F29.imprint","IMPRINT",FACE,{"disambiguationData":[TD([[makeQuery(id+"F29.imprint","IMPRINT",EDGE,{"derivedFrom":sQuery(id+"F29.wireOp",EDGE,"E60.0")}),-1.0]])]});
            extrude(context, id + "F30", {"entities" : qUnion([Q0]), "operationType" : NewBodyOperationType.ADD, "oppositeDirection" : true, "depth" : 12.7 * mm});
        }
    });
